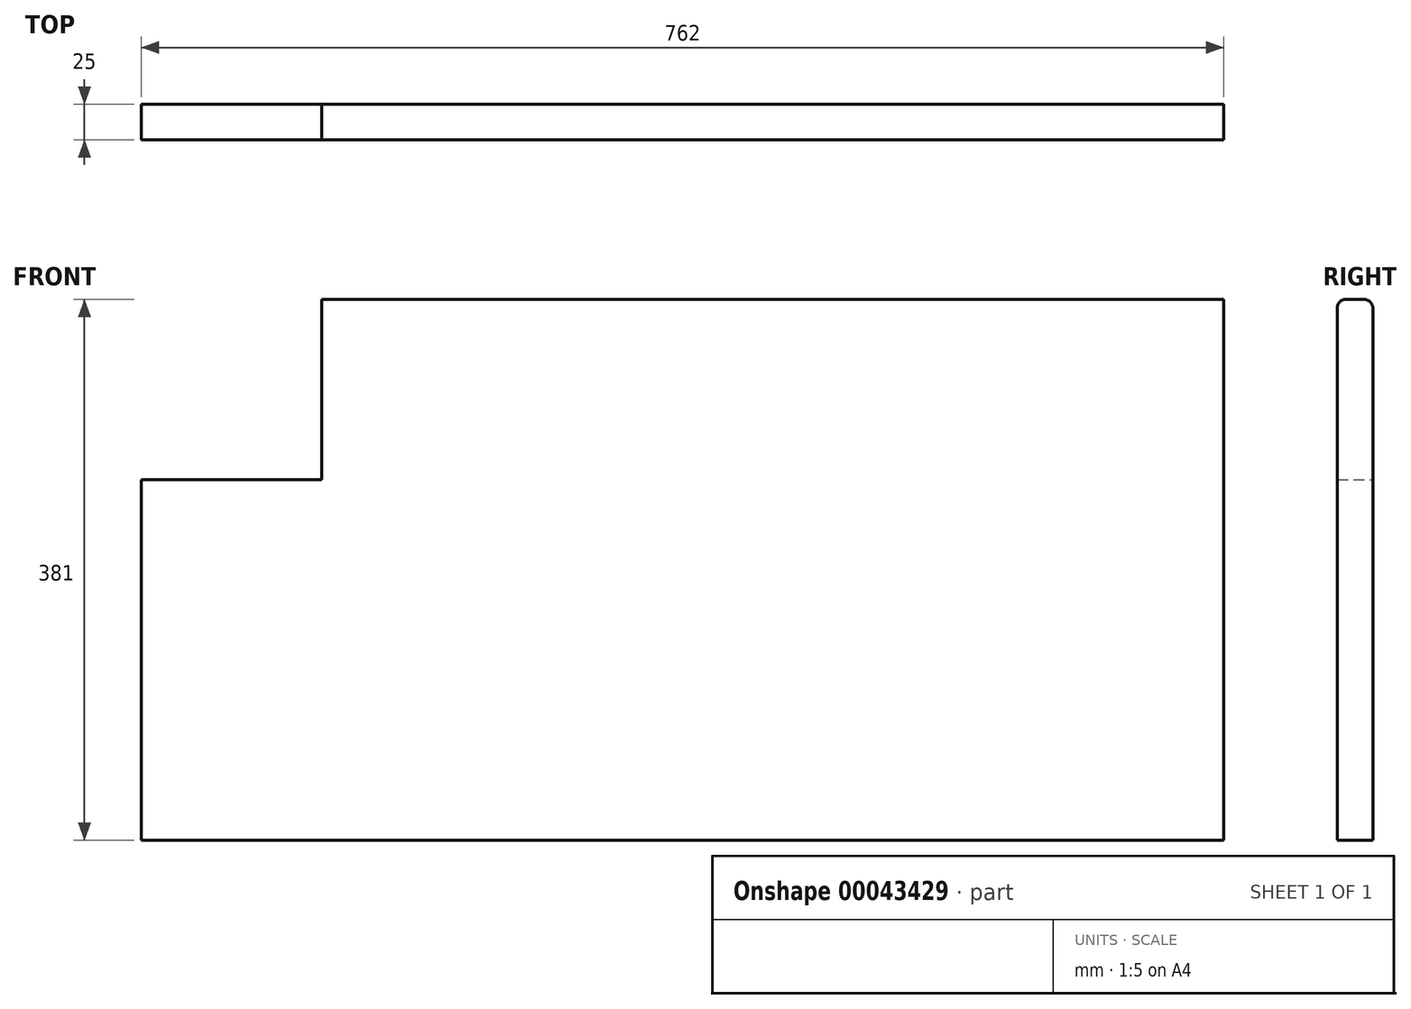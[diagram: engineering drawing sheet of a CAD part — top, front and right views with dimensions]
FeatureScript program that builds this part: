
annotation { "Feature Type Name" : "Feature", "Feature Type Description" : "" }
export const myFeature = defineFeature(function(context is Context, id is Id, definition is map)
    precondition{}
    {
        {
            var Q0;
            Q0=qCreatedBy(makeId("Front.planeOp"),FACE);
            var sketch = newSketch(context, id + "F0", { "sketchPlane" : qUnion([Q0])});
            skLineSegment(sketch, "E0.bottom", {"start": v(-762, 381) * mm, "end": v(0, 381) * mm});
            skLineSegment(sketch, "E0.top", {"start": v(-762, 0) * mm, "end": v(0, 0) * mm});
            skLineSegment(sketch, "E0.left", {"start": v(-762, 381) * mm, "end": v(-762, 0) * mm});
            skLineSegment(sketch, "E0.right", {"start": v(0, 381) * mm, "end": v(0, 0) * mm});
            skLineSegment(sketch, "E1", {"start": v(-635, 254) * mm, "end": v(-762, 254) * mm});
            skLineSegment(sketch, "E2", {"start": v(-635, 254) * mm, "end": v(-635, 381) * mm});
            skSolve(sketch);
        }
        {
            var Q0;
            {var subQ4=sQuery(id+"F0.wireOp",EDGE,"E0.top");Q0=makeQuery(id+"F0.imprint","IMPRINT",FACE,{"disambiguationData":[TD([[makeQuery(id+"F0.imprint","IMPRINT",EDGE,{"derivedFrom":subQ4}),1.0]])]});}
            extrude(context, id + "F1", {"entities" : qUnion([Q0]), "depth" : 25 * mm});
        }
        {
            var Q0;
            Q0=makeQuery(id+"F1.opExtrude","CAP_EDGE",EDGE,{"disambiguationData":[OSD([sQuery(id+"F0.wireOp",EDGE,"E0.bottom")])],"isStart":false});
            fillet(context, id + "F2", {"entities" : qUnion([Q0]), "radius" : 6 * mm, "tangentPropagation" : true, "allowEdgeOverflow" : false});
        }
        {
            var Q0;
            Q0=makeQuery(id+"F1.opExtrude","CAP_EDGE",EDGE,{"disambiguationData":[OSD([sQuery(id+"F0.wireOp",EDGE,"E0.bottom")])],"isStart":true});
            fillet(context, id + "F3", {"entities" : qUnion([Q0]), "radius" : 6 * mm, "tangentPropagation" : true, "allowEdgeOverflow" : false});
        }
    });
